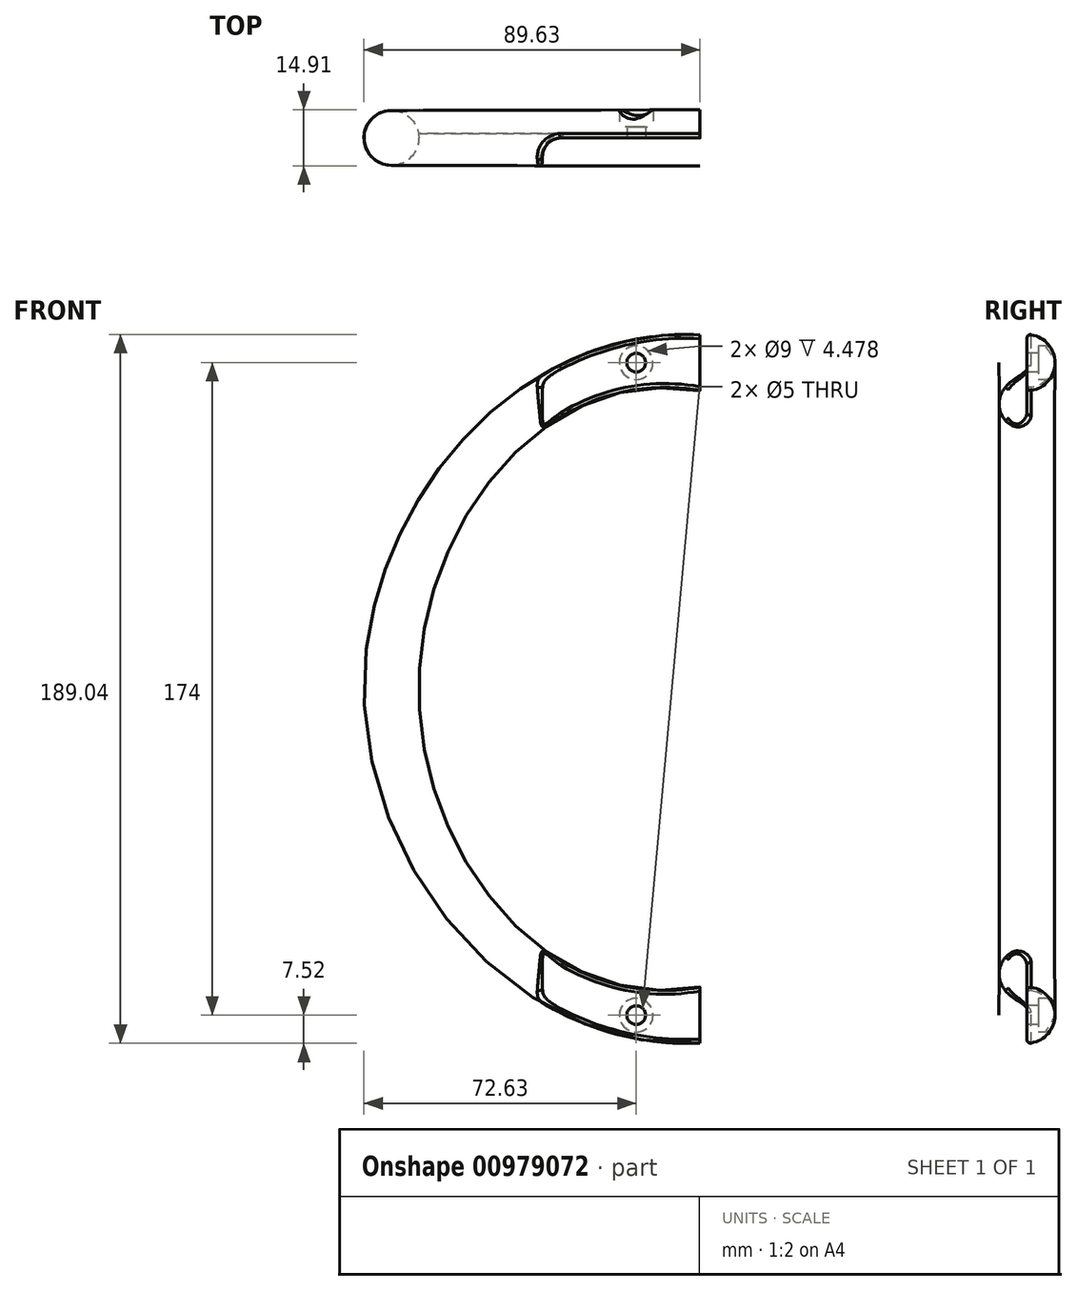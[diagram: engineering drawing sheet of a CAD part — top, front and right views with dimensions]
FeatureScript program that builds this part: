
annotation { "Feature Type Name" : "Feature", "Feature Type Description" : "" }
export const myFeature = defineFeature(function(context is Context, id is Id, definition is map)
    precondition{}
    {
        {
            var Q0;
            Q0=qCreatedBy(makeId("Right.planeOp"),FACE);
            var sketch = newSketch(context, id + "F0", { "sketchPlane" : qUnion([Q0])});
            skCircle(sketch, "E0", {"center": v(0, 0) * mm, "radius": 7.5 * mm});
            skCircle(sketch, "E1", {"center": v(0, 174) * mm, "radius": 7.5 * mm});
            skLineSegment(sketch, "E2", {"start": v(0, 0) * mm, "end": v(0, 7.5) * mm, "construction": true});
            skLineSegment(sketch, "E3", {"start": v(0, 174) * mm, "end": v(0, 181.5) * mm, "construction": true});
            skLineSegment(sketch, "E4", {"start": v(0, 174) * mm, "end": v(0, 166.5) * mm, "construction": true});
            skSolve(sketch);
        }
        {
            var Q0;
            Q0=qCreatedBy(makeId("Top.planeOp"),FACE);
            cPlane(context, id + "F1", {"entities" : qUnion([Q0]), "cplaneType" : CPlaneType.OFFSET, "offset" : 87 * mm, "width" : 150 * mm, "height" : 150 * mm});
        }
        {
            var Q0;
            Q0=qCreatedBy(id+"F1.planeOp",FACE);
            var sketch = newSketch(context, id + "F2", { "sketchPlane" : qUnion([Q0])});
            skLineSegment(sketch, "E5", {"start": v(0, 0) * mm, "end": v(-75, 0) * mm, "construction": true});
            skCircle(sketch, "E6", {"center": v(-82.32, 0) * mm, "radius": 7.32 * mm});
            skLineSegment(sketch, "E7", {"start": v(-75, 0) * mm, "end": v(-82.32, 0) * mm, "construction": true});
            skSolve(sketch);
        }
        {
            var Q0;
            Q0=sQuery(id+"F0.wireOp",VERTEX,"E1.center");
            var Q1;
            Q1=sQuery(id+"F2.wireOp",VERTEX,"E5.end");
            var Q2;
            Q2=sQuery(id+"F0.wireOp",VERTEX,"E0.center");
            cPlane(context, id + "F3", {"entities" : qUnion([Q0, Q1, Q2]), "cplaneType" : CPlaneType.THREE_POINT, "offset" : 25 * mm, "width" : 150 * mm, "height" : 150 * mm});
        }
        {
            var Q0;
            Q0=qCreatedBy(id+"F3.planeOp",FACE);
            var sketch = newSketch(context, id + "F4", { "sketchPlane" : qUnion([Q0])});
            skFitSpline(sketch, "E8", {"points": [v(0, 166.5) * mm, v(75, 87) * mm, v(0, 7.5) * mm], "startDerivative": vector(252, 45) * mm, "endDerivative": vector(-252, 45) * mm});
            skLineSegment(sketch, "E9", {"start": v(0, 0) * mm, "end": v(17, 0) * mm, "construction": true});
            skLineSegment(sketch, "E10", {"start": v(17, 0) * mm, "end": v(42, 0) * mm, "construction": true});
            skLineSegment(sketch, "E11", {"start": v(42, 0) * mm, "end": v(75, 0) * mm, "construction": true});
            skLineSegment(sketch, "E12", {"start": v(42, 0) * mm, "end": v(42, 174) * mm, "construction": true});
            skCircle(sketch, "E13", {"center": v(17, 0) * mm, "radius": 2.5 * mm});
            skCircle(sketch, "E14", {"center": v(17, 0) * mm, "radius": 4.5 * mm});
            skCircle(sketch, "E15", {"center": v(17, 174) * mm, "radius": 2.5 * mm});
            skCircle(sketch, "E16", {"center": v(17, 174) * mm, "radius": 4.5 * mm});
            skText(sketch, "E17", { "text": "COWO", "fontName": "OpenSans-Regular.ttf"});
            const initialGuessF4  = {"E17": [0.06562, 0.0299, 0.29792, 0.9546, 0.01253]};
            skSetInitialGuess(sketch, initialGuessF4);
            skSolve(sketch);
        }
        {
            var Q0;
            Q0=makeQuery(id+"F0.imprint","IMPRINT",FACE,{"disambiguationData":[TD([[makeQuery(id+"F0.imprint","IMPRINT",EDGE,{"derivedFrom":sQuery(id+"F0.wireOp",EDGE,"E0")}),1.0]])]});
            var Q1;
            Q1=makeQuery(id+"F2.imprint","IMPRINT",FACE,{"disambiguationData":[TD([[makeQuery(id+"F2.imprint","IMPRINT",EDGE,{"derivedFrom":sQuery(id+"F2.wireOp",EDGE,"E6")}),1.0]])]});
            var Q2;
            Q2=makeQuery(id+"F0.imprint","IMPRINT",FACE,{"disambiguationData":[TD([[makeQuery(id+"F0.imprint","IMPRINT",EDGE,{"derivedFrom":sQuery(id+"F0.wireOp",EDGE,"E1")}),1.0]])]});
            var Q3;
            Q3=sQuery(id+"F4.wireOp",EDGE,"E8");
            loft(context, id + "F5", {"addGuides" : true, "sheetProfilesArray" : [{ "sheetProfileEntities" : qUnion([Q0]) }, { "sheetProfileEntities" : qUnion([Q1]) }, { "sheetProfileEntities" : qUnion([Q2]) }], "guidesArray" : [{ "guideEntities" : qUnion([Q3]), "guideDerivativeType" : LoftGuideDerivativeType.DEFAULT, "guideDerivativeMagnitude" : 1 }]});
        }
        {
            var Q0;
            Q0=qCreatedBy(makeId("Right.planeOp"),FACE);
            var sketch = newSketch(context, id + "F6", { "sketchPlane" : qUnion([Q0])});
            skLineSegment(sketch, "E18", {"start": v(0, -12.46) * mm, "end": v(0, 185.4) * mm});
            skLineSegment(sketch, "E19", {"start": v(0, 185.4) * mm, "end": v(-18.53, 185.4) * mm});
            skLineSegment(sketch, "E20", {"start": v(-18.53, 185.4) * mm, "end": v(-18.53, -12.46) * mm});
            skLineSegment(sketch, "E21", {"start": v(-18.53, -12.46) * mm, "end": v(0, -12.46) * mm});
            skSolve(sketch);
        }
        {
            var Q0;
            Q0=makeQuery(id+"F6.imprint","IMPRINT",FACE,{"disambiguationData":[TD([[makeQuery(id+"F6.imprint","IMPRINT",EDGE,{"derivedFrom":sQuery(id+"F6.wireOp",EDGE,"E18")}),1.0]])]});
            extrude(context, id + "F7", {"entities" : qUnion([Q0]), "operationType" : NewBodyOperationType.REMOVE, "oppositeDirection" : true, "depth" : 42 * mm, "offsetDistance" : 25 * mm});
        }
        {
            var Q0;
            Q0=makeQuery(id+"F4.imprint","IMPRINT",FACE,{"disambiguationData":[TD([[makeQuery(id+"F4.imprint","IMPRINT",EDGE,{"derivedFrom":sQuery(id+"F4.wireOp",EDGE,"E15")}),1.0]])]});
            var Q1;
            Q1=makeQuery(id+"F4.imprint","IMPRINT",FACE,{"disambiguationData":[TD([[makeQuery(id+"F4.imprint","IMPRINT",EDGE,{"derivedFrom":sQuery(id+"F4.wireOp",EDGE,"E13")}),1.0]])]});
            var Q2;
            Q2=makeQuery(id+"F4.imprint","IMPRINT",FACE,{"disambiguationData":[TD([[makeQuery(id+"F4.imprint","IMPRINT",EDGE,{"derivedFrom":sQuery(id+"F4.wireOp",EDGE,"E13")}),-1.0]])]});
            var Q3;
            Q3=makeQuery(id+"F4.imprint","IMPRINT",FACE,{"disambiguationData":[TD([[makeQuery(id+"F4.imprint","IMPRINT",EDGE,{"derivedFrom":sQuery(id+"F4.wireOp",EDGE,"E15")}),-1.0]])]});
            extrude(context, id + "F8", {"entities" : qUnion([Q0, Q1, Q2, Q3]), "operationType" : NewBodyOperationType.REMOVE, "endBound" : BoundingType.THROUGH_ALL, "depth" : 25 * mm, "offsetDistance" : 25 * mm});
        }
        {
            var Q0;
            Q0=makeQuery(id+"F4.imprint","IMPRINT",FACE,{"disambiguationData":[TD([[makeQuery(id+"F4.imprint","IMPRINT",EDGE,{"derivedFrom":sQuery(id+"F4.wireOp",EDGE,"E13")}),-1.0]])]});
            var Q1;
            Q1=makeQuery(id+"F4.imprint","IMPRINT",FACE,{"disambiguationData":[TD([[makeQuery(id+"F4.imprint","IMPRINT",EDGE,{"derivedFrom":sQuery(id+"F4.wireOp",EDGE,"E15")}),-1.0]])]});
            extrude(context, id + "F9", {"entities" : qUnion([Q0, Q1]), "operationType" : NewBodyOperationType.ADD, "depth" : 3 * mm, "offsetDistance" : 25 * mm});
        }
        {
            var Q0;
            Q0=makeQuery(id+"F7.boolean.opBoolean","COPY",EDGE,{"disambiguationData":[OD(0.0)],"derivedFrom":makeQuery(id+"F7.opExtrude","CAP_EDGE",EDGE,{"disambiguationData":[OSD([sQuery(id+"F6.wireOp",EDGE,"E18")])],"isStart":false})});
            var Q1;
            Q1=makeQuery(id+"F7.boolean.opBoolean","COPY",EDGE,{"disambiguationData":[OD(1.0)],"derivedFrom":makeQuery(id+"F7.opExtrude","CAP_EDGE",EDGE,{"disambiguationData":[OSD([sQuery(id+"F6.wireOp",EDGE,"E18")])],"isStart":false})});
            var Q2;
            {var subQ0=sQuery(id+"F6.wireOp",EDGE,"E18");Q2=makeQuery(id+"F7.boolean.opBoolean","COPY",EDGE,{"disambiguationData":[topologyDisambiguationEdgeConnected([makeQuery(id+"F5.opLoft","CAP_FACE",FACE,{"disambiguationData":[OSD([makeQuery(id+"F0.imprint","IMPRINT",FACE,{"disambiguationData":[TD([[makeQuery(id+"F0.imprint","IMPRINT",EDGE,{"derivedFrom":sQuery(id+"F0.wireOp",EDGE,"E1")}),1.0]])]})])],"isStart":true})])],"derivedFrom":makeQuery(id+"F7.opExtrude","CAP_EDGE",EDGE,{"disambiguationData":[OSD([subQ0])],"isStart":true})});}
            var Q3;
            {var subQ0=sQuery(id+"F6.wireOp",EDGE,"E18");Q3=makeQuery(id+"F7.boolean.opBoolean","COPY",EDGE,{"disambiguationData":[topologyDisambiguationEdgeConnected([makeQuery(id+"F5.opLoft","CAP_FACE",FACE,{"disambiguationData":[OSD([makeQuery(id+"F0.imprint","IMPRINT",FACE,{"disambiguationData":[TD([[makeQuery(id+"F0.imprint","IMPRINT",EDGE,{"derivedFrom":sQuery(id+"F0.wireOp",EDGE,"E0")}),1.0]])]})])],"isStart":true})])],"derivedFrom":makeQuery(id+"F7.opExtrude","CAP_EDGE",EDGE,{"disambiguationData":[OSD([subQ0])],"isStart":true})});}
            fillet(context, id + "F10", {"entities" : qUnion([Q0, Q1, Q2, Q3]), "radius" : 5 * mm, "tangentPropagation" : true, "allowEdgeOverflow" : false});
        }
        {
            var Q0;
            Q0=makeQuery(id+"F7.boolean.opBoolean","INTERSECT",EDGE,{"disambiguationData":[OD(0.0)],"derivedFrom":[makeQuery(id+"F5.opLoft","SWEPT_FACE",FACE,{"disambiguationData":[OSD([sQuery(id+"F0.wireOp",EDGE,"E0"),sQuery(id+"F0.wireOp",EDGE,"E1"),sQuery(id+"F2.wireOp",EDGE,"E6"),sQuery(id+"F4.wireOp",VERTEX,"E8.start"),sQuery(id+"F4.wireOp",VERTEX,"E8.end"),sQuery(id+"F4.wireOp",EDGE,"E8")])]}),makeQuery(id+"F7.opExtrude","CAP_FACE",FACE,{"disambiguationData":[OSD([sQuery(id+"F6.wireOp",EDGE,"E18"),sQuery(id+"F6.wireOp",EDGE,"E19"),sQuery(id+"F6.wireOp",EDGE,"E20"),sQuery(id+"F6.wireOp",EDGE,"E21")])],"isStart":false})]});
            var Q1;
            Q1=makeQuery(id+"F7.boolean.opBoolean","INTERSECT",EDGE,{"disambiguationData":[OD(1.0)],"derivedFrom":[makeQuery(id+"F5.opLoft","SWEPT_FACE",FACE,{"disambiguationData":[OSD([sQuery(id+"F0.wireOp",EDGE,"E0"),sQuery(id+"F0.wireOp",EDGE,"E1"),sQuery(id+"F2.wireOp",EDGE,"E6"),sQuery(id+"F4.wireOp",VERTEX,"E8.start"),sQuery(id+"F4.wireOp",VERTEX,"E8.end"),sQuery(id+"F4.wireOp",EDGE,"E8")])]}),makeQuery(id+"F7.opExtrude","CAP_FACE",FACE,{"disambiguationData":[OSD([sQuery(id+"F6.wireOp",EDGE,"E18"),sQuery(id+"F6.wireOp",EDGE,"E19"),sQuery(id+"F6.wireOp",EDGE,"E20"),sQuery(id+"F6.wireOp",EDGE,"E21")])],"isStart":false})]});
            fillet(context, id + "F11", {"entities" : qUnion([Q0, Q1]), "radius" : 1 * mm, "tangentPropagation" : true, "allowEdgeOverflow" : false});
        }
    });
